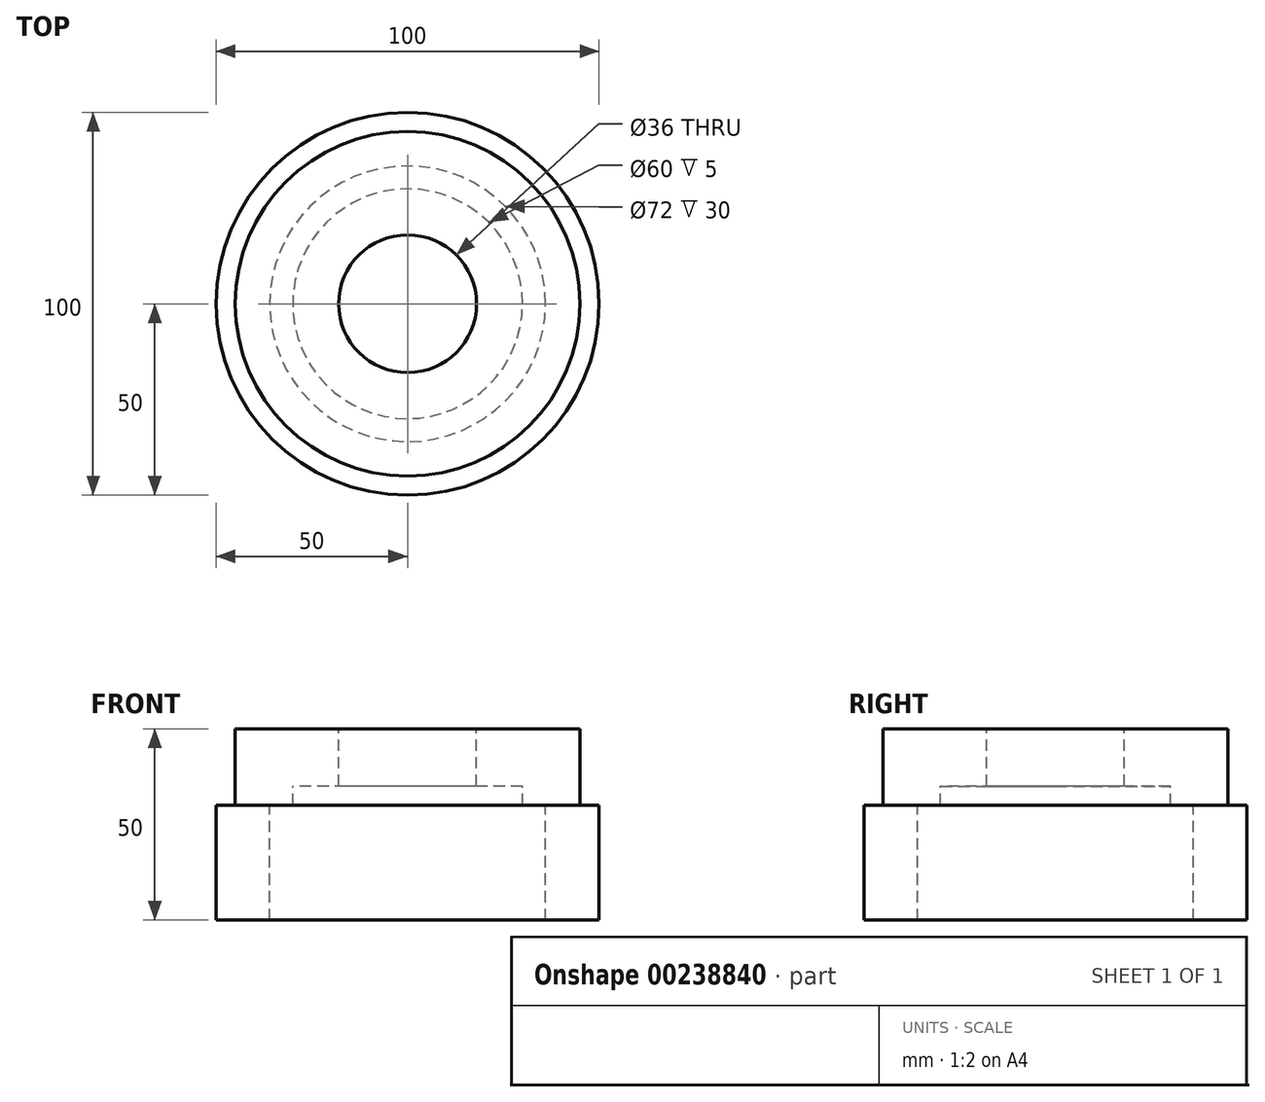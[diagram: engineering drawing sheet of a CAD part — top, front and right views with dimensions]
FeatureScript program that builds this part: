
annotation { "Feature Type Name" : "Feature", "Feature Type Description" : "" }
export const myFeature = defineFeature(function(context is Context, id is Id, definition is map)
    precondition{}
    {
        {
            var Q0;
            Q0=qCreatedBy(makeId("Front.planeOp"),FACE);
            var sketch = newSketch(context, id + "F0", { "sketchPlane" : qUnion([Q0])});
            skLineSegment(sketch, "E0", {"start": v(0, 45.91) * mm, "end": v(0, -52.3) * mm, "construction": true});
            skLineSegment(sketch, "E1", {"start": v(18, 43.43) * mm, "end": v(45, 43.43) * mm});
            skLineSegment(sketch, "E2", {"start": v(45, 43.43) * mm, "end": v(45, 23.43) * mm});
            skLineSegment(sketch, "E3", {"start": v(45, 23.43) * mm, "end": v(50, 23.43) * mm});
            skLineSegment(sketch, "E4", {"start": v(50, 23.43) * mm, "end": v(50, -6.57) * mm});
            skLineSegment(sketch, "E5", {"start": v(50, -6.57) * mm, "end": v(36, -6.57) * mm});
            skLineSegment(sketch, "E6", {"start": v(36, -6.57) * mm, "end": v(36, 23.43) * mm});
            skLineSegment(sketch, "E7", {"start": v(36, 23.43) * mm, "end": v(30, 23.43) * mm});
            skLineSegment(sketch, "E8", {"start": v(30, 23.43) * mm, "end": v(30, 28.43) * mm});
            skLineSegment(sketch, "E9", {"start": v(30, 28.43) * mm, "end": v(18, 28.43) * mm});
            skLineSegment(sketch, "E10", {"start": v(18, 28.43) * mm, "end": v(18, 43.43) * mm});
            skSolve(sketch);
        }
        {
            var Q0;
            Q0=makeQuery(id+"F0.imprint","IMPRINT",FACE,{"disambiguationData":[TD([[makeQuery(id+"F0.imprint","IMPRINT",EDGE,{"derivedFrom":sQuery(id+"F0.wireOp",EDGE,"E1")}),-1.0]])]});
            var Q1;
            Q1=sQuery(id+"F0.wireOp",EDGE,"E0");
            revolve(context, id + "F1", {"entities" : qUnion([Q0]), "axis" : qUnion([Q1]), "revolveType" : RevolveType.FULL});
        }
    });
